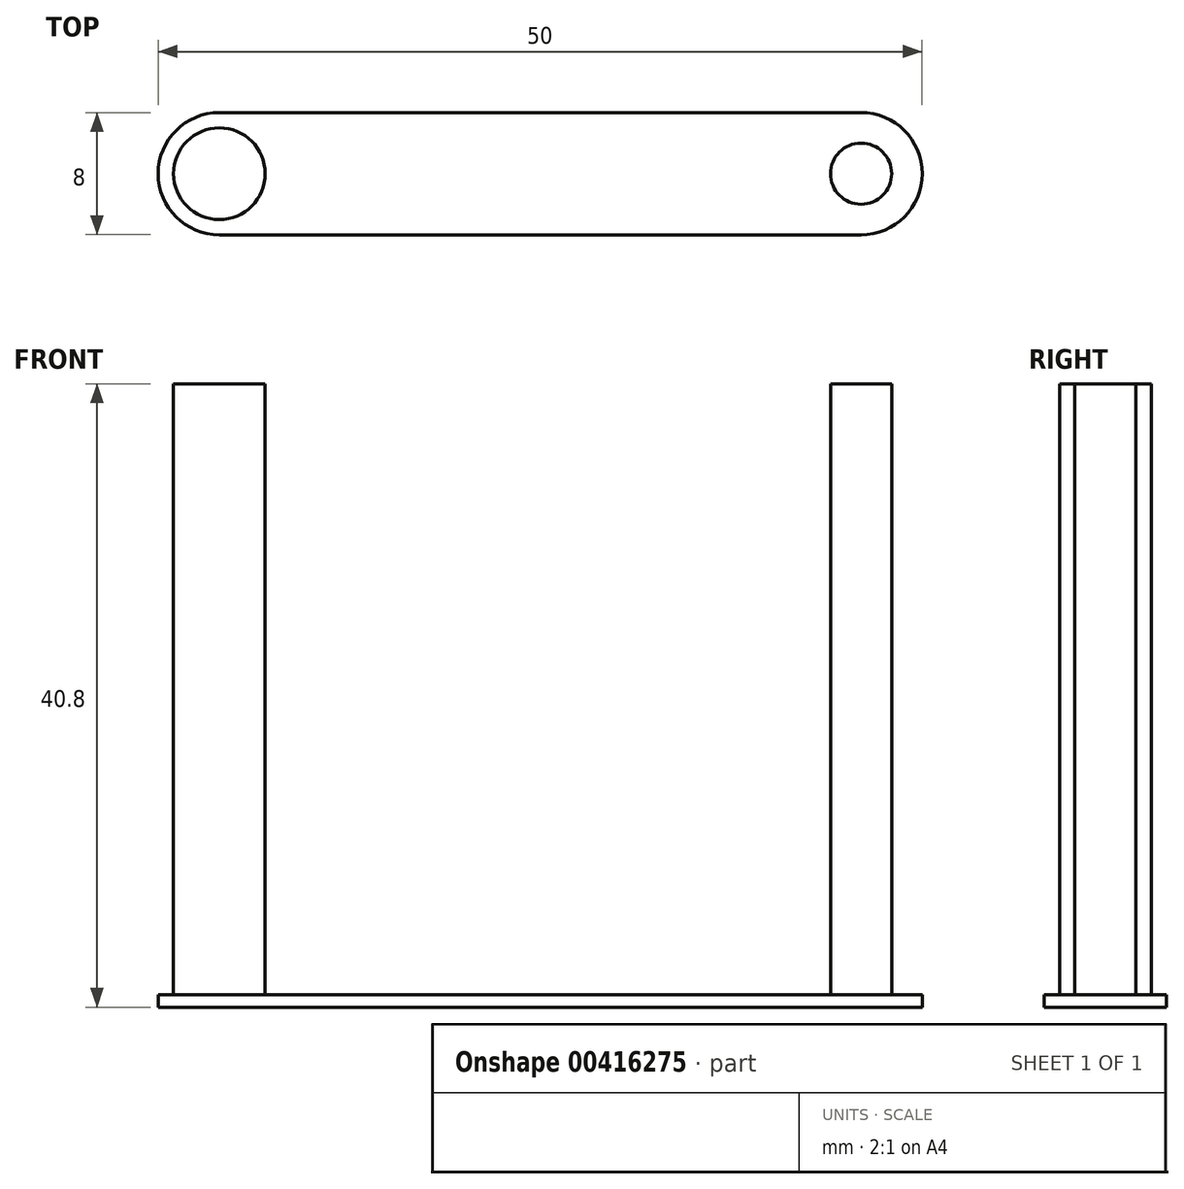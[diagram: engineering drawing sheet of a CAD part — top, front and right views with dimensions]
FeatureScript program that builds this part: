
annotation { "Feature Type Name" : "Feature", "Feature Type Description" : "" }
export const myFeature = defineFeature(function(context is Context, id is Id, definition is map)
    precondition{}
    {
        {
            var Q0;
            Q0=qCreatedBy(makeId("Top.planeOp"),FACE);
            var sketch = newSketch(context, id + "F0", { "sketchPlane" : qUnion([Q0])});
            skLineSegment(sketch, "E0.bottom", {"start": v(-14.37, 3.1) * mm, "end": v(27.63, 3.1) * mm});
            skLineSegment(sketch, "E0.top", {"start": v(-14.37, -4.9) * mm, "end": v(27.63, -4.9) * mm});
            skLineSegment(sketch, "E0.left", {"start": v(-18.37, -0.9) * mm, "end": v(-18.37, -0.9) * mm});
            skLineSegment(sketch, "E0.right", {"start": v(31.63, -0.9) * mm, "end": v(31.63, -0.9) * mm});
            skPoint(sketch, "E1.visualSharp", {"position": v(-18.37, 3.1) * mm});
            skArc(sketch, "E1.filletArc", {"start": v(-14.37, 3.1) * mm, "mid": v(-17.2, 1.92) * mm, "end": v(-18.37, -0.9) * mm});
            skPoint(sketch, "E2.visualSharp", {"position": v(-18.37, -4.9) * mm});
            skArc(sketch, "E2.filletArc", {"start": v(-18.37, -0.9) * mm, "mid": v(-17.2, -3.73) * mm, "end": v(-14.37, -4.9) * mm});
            skPoint(sketch, "E3.visualSharp", {"position": v(31.63, 3.1) * mm});
            skArc(sketch, "E3.filletArc", {"start": v(31.63, -0.9) * mm, "mid": v(30.46, 1.92) * mm, "end": v(27.63, 3.1) * mm});
            skPoint(sketch, "E4.visualSharp", {"position": v(31.63, -4.9) * mm});
            skArc(sketch, "E4.filletArc", {"start": v(27.63, -4.9) * mm, "mid": v(30.46, -3.73) * mm, "end": v(31.63, -0.9) * mm});
            skSolve(sketch);
        }
        {
            var Q0;
            Q0=makeQuery(id+"F0.imprint","IMPRINT",FACE,{"disambiguationData":[TD([[makeQuery(id+"F0.imprint","IMPRINT",EDGE,{"derivedFrom":sQuery(id+"F0.wireOp",EDGE,"E0.bottom")}),-1.0]])]});
            extrude(context, id + "F1", {"entities" : qUnion([Q0]), "depth" : .8 * mm});
        }
        {
            var Q0;
            Q0=makeQuery(id+"F1.opExtrude","CAP_FACE",FACE,{"disambiguationData":[OSD([sQuery(id+"F0.wireOp",EDGE,"E0.bottom"),sQuery(id+"F0.wireOp",EDGE,"E0.top"),sQuery(id+"F0.wireOp",EDGE,"E1.filletArc"),sQuery(id+"F0.wireOp",EDGE,"E2.filletArc"),sQuery(id+"F0.wireOp",EDGE,"E3.filletArc"),sQuery(id+"F0.wireOp",EDGE,"E4.filletArc")])],"isStart":false});
            var sketch = newSketch(context, id + "F2", { "sketchPlane" : qUnion([Q0])});
            skCircle(sketch, "E5", {"center": v(-14.37, -0.9) * mm, "radius": 3 * mm});
            skCircle(sketch, "E6", {"center": v(27.63, -0.9) * mm, "radius": 2 * mm});
            skSolve(sketch);
        }
        {
            var Q0;
            Q0=makeQuery(id+"F2.imprint","IMPRINT",FACE,{"disambiguationData":[TD([[makeQuery(id+"F2.imprint","IMPRINT",EDGE,{"derivedFrom":sQuery(id+"F2.wireOp",EDGE,"E5")}),1.0]])]});
            var Q1;
            Q1=makeQuery(id+"F2.imprint","IMPRINT",FACE,{"disambiguationData":[TD([[makeQuery(id+"F2.imprint","IMPRINT",EDGE,{"derivedFrom":sQuery(id+"F2.wireOp",EDGE,"E6")}),1.0]])]});
            extrude(context, id + "F3", {"entities" : qUnion([Q0, Q1]), "operationType" : NewBodyOperationType.ADD, "depth" : 40 * mm});
        }
    });
